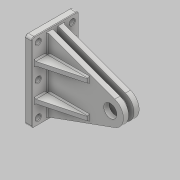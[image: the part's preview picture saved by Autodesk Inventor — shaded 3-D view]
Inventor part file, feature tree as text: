
AUTODESK INVENTOR PART (.ipt)
format: ipt  version: 2018 (Build 220112000, 112)  size: 245,760 bytes
history: native  units: mm
features: plane x5, sketch x4, extrude x3, chamfer x3, mirror x3, other x2, fillet x1, hole x1, pattern_linear x1
ambient origin geometry x8: Origin, YZ Plane, XZ Plane, XY Plane, X Axis, Y Axis, Z Axis, Center Point
bodies: Body1 (feature_tree)
feature tree (23):
  other  "實體1"
  extrude  "擠出1"  Depth=180.0mm
  fillet  "圓角1"  Radius=300.0mm
  chamfer  "倒角1"  Distance=25.0mm
  hole  "孔1"  [1 undecoded]
  chamfer  "倒角2"  Distance=2.0mm Angle=45.0deg
  pattern_linear  "矩形陣列1"  Spacing1=125.0mm  [1 undecoded]
  plane  "工作平面1"
  mirror  "鏡射1"
  plane  "工作平面3"
  extrude  "擠出2"  Depth=65.0mm
  plane  "工作平面5"
  extrude  "擠出3"  Depth=2.0mm TaperAngle=45.0deg
  mirror  "鏡射2"
  mirror  "鏡射3"
  chamfer  "倒角3"  Distance=125.0mm
  sketch  "草圖1"
  sketch  "草圖2"
  plane  "工作平面2"
  sketch  "草圖3"
  other  "工作軸線1"
  plane  "工作平面4"
  sketch  "草圖4"
note: 2 required parameter values undecoded (feature->parameter linkage not recoverable at this tier; creation-order binding heuristic only, values carry confidence <= 0.55)
